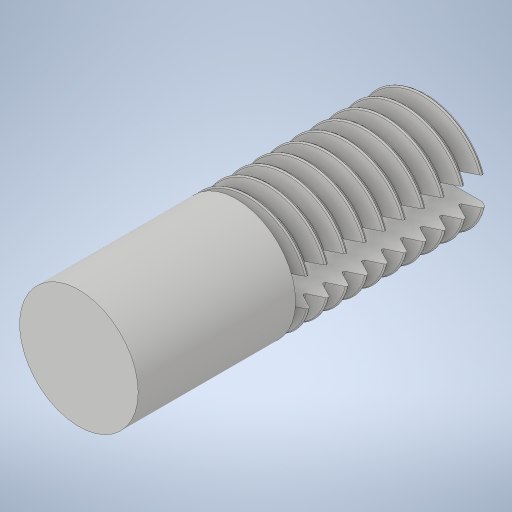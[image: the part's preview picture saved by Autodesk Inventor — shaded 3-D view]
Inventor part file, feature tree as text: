
AUTODESK INVENTOR PART (.ipt)
format: ipt  version: 2023 (Build 270158000, 158)  size: 1,039,360 bytes
history: native  units: mm
features: sketch x5, extrude x2, revolve x2, thread x1, helix x1, boolean_combine x1
ambient origin geometry x8: Origin, YZ Plane, XZ Plane, XY Plane, X Axis, Y Axis, Z Axis, Center Point
bodies: Solid1 (feature_tree), Solid2 (feature_tree)
feature tree (12):
  extrude  "Extrusion1"  Depth=18.1mm TaperAngle=0.0deg
  thread  "Thread1"  [1 undecoded]
  revolve  "Revolution1"  [1 undecoded]
  revolve  "Revolution2"  [1 undecoded]
  helix  "Coil1"  [1 undecoded]
  sketch  "Sketch5"  dims[d25=10.0mm d26=0.0mm d27=8.0mm]
  boolean_combine  "Combine1"
  extrude  "Extrusion2"  Depth=1.5mm
  sketch  "Sketch1"  dims[d0=6.1mm d1=18.1mm d2=0.0mm d3=10.0mm d4=0.0mm]
  sketch  "Sketch2"  dims[d5=9.599311mm d6=0.160083mm d7=0.160083mm d10=1.0mm]
  sketch  "Sketch3"  dims[d12=9.599311mm d14=0.0mm d15=0.0mm]
  sketch  "Sketch4"  dims[d16=1.001mm d17=12.0mm d18=10.0mm d19=0.0mm d20=0.0mm d21=0.0mm d22=0.0mm d23=0.0mm d24=1.5mm]
note: 4 required parameter values undecoded (feature->parameter linkage not recoverable at this tier; creation-order binding heuristic only, values carry confidence <= 0.55)